# Revit family: WM-MN Skimmend 25mm Family
name_source: partatom
category: Generic Models
revit_build: Autodesk Revit 2017 (Build: 20160225_1515(x64)
units: mm (PartAtom-declared; Revit-internal decimal feet)

## family parameters
Always vertical = Yes
Can host rebar = No
Cut with Voids When Loaded = No
Host = Ceiling
Part Type = Normal
Room Calculation Point = No
Round Connector Dimension = Use Diameter
Shared = No

## types (1)
- Lamdaboard
    Density = 40.0000 kg/m³
    Description = Flexible PIR Insulation
    Manufacturer = Lambdaboard
    Model = WM/MN Skimmend 25mm
    Thermal Conductivity = 0.0240 W/(m·K)
    Thermal Resistance = 1.0400 (m²·K)/W
    URL = www.rigifoam.com
    lenght = 4000 mm  [stored 13.1234 ft]
    material = White
    thickness = 25 mm  [stored 0.082021 ft]
    width = 4000 mm  [stored 13.1234 ft]

note: [stored X ft] marks values corroborated as IEEE doubles in the binary element streams (Revit-internal decimal feet)

## geometry (parser evidence)
native form markers: Sweep x2
no freeform markers — native parametric forms only
